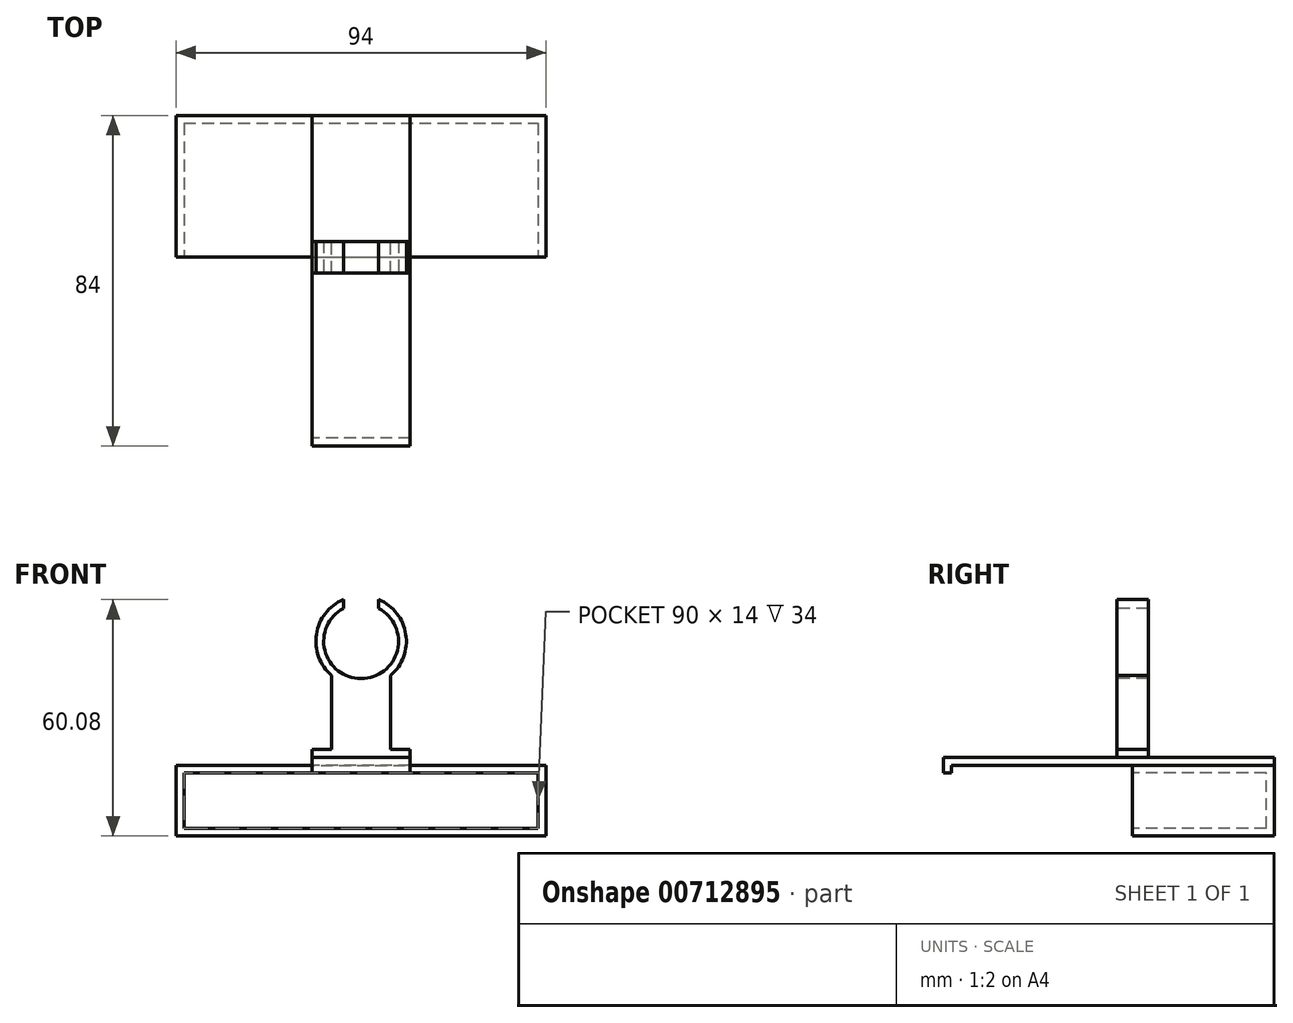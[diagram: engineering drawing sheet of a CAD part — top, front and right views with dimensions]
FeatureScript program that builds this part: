
annotation { "Feature Type Name" : "Feature", "Feature Type Description" : "" }
export const myFeature = defineFeature(function(context is Context, id is Id, definition is map)
    precondition{}
    {
        {
            var Q0;
            Q0=qCreatedBy(makeId("Front.planeOp"),FACE);
            var sketch = newSketch(context, id + "F0", { "sketchPlane" : qUnion([Q0])});
            skLineSegment(sketch, "E0.bottom", {"start": v(-47, 0) * mm, "end": v(47, 0) * mm});
            skLineSegment(sketch, "E0.top", {"start": v(-47, 18) * mm, "end": v(47, 18) * mm});
            skLineSegment(sketch, "E0.left", {"start": v(-47, 0) * mm, "end": v(-47, 18) * mm});
            skLineSegment(sketch, "E0.right", {"start": v(47, 0) * mm, "end": v(47, 18) * mm});
            skSolve(sketch);
        }
        {
            var Q0;
            Q0=makeQuery(id+"F0.imprint","IMPRINT",FACE,{"disambiguationData":[TD([[makeQuery(id+"F0.imprint","IMPRINT",EDGE,{"derivedFrom":sQuery(id+"F0.wireOp",EDGE,"E0.bottom")}),1.0]])]});
            extrude(context, id + "F1", {"entities" : qUnion([Q0]), "oppositeDirection" : true, "depth" : 36 * mm, "offsetDistance" : 25 * mm});
        }
        {
            var Q0;
            Q0=makeQuery(id+"F1.opExtrude","CAP_FACE",FACE,{"disambiguationData":[OSD([sQuery(id+"F0.wireOp",EDGE,"E0.bottom"),sQuery(id+"F0.wireOp",EDGE,"E0.top"),sQuery(id+"F0.wireOp",EDGE,"E0.left"),sQuery(id+"F0.wireOp",EDGE,"E0.right")])],"isStart":true});
            shell(context, id + "F2", {"entities" : qUnion([Q0]), "thickness" : 2 * mm});
        }
        {
            var Q0;
            Q0=qCreatedBy(makeId("Right.planeOp"),FACE);
            var sketch = newSketch(context, id + "F3", { "sketchPlane" : qUnion([Q0])});
            skLineSegment(sketch, "E1.0", {"start": v(36, 18) * mm, "end": v(0, 18) * mm});
            skLineSegment(sketch, "E2.0.1", {"start": v(0, 18) * mm, "end": v(36, 18) * mm});
            skLineSegment(sketch, "E3.bottom", {"start": v(36, 18) * mm, "end": v(-44.7, 18) * mm});
            skLineSegment(sketch, "E3.top", {"start": v(36, 20) * mm, "end": v(-48, 20) * mm});
            skLineSegment(sketch, "E3.left", {"start": v(36, 18) * mm, "end": v(36, 20) * mm});
            skLineSegment(sketch, "E3.right", {"start": v(-48, 18) * mm, "end": v(-48, 20) * mm});
            skLineSegment(sketch, "E4.top", {"start": v(-48, 16) * mm, "end": v(-46, 16) * mm});
            skLineSegment(sketch, "E4.left", {"start": v(-48, 18) * mm, "end": v(-48, 16) * mm});
            skLineSegment(sketch, "E4.right", {"start": v(-46, 18) * mm, "end": v(-46, 17) * mm});
            skLineSegment(sketch, "E5", {"start": v(-44.7, 18) * mm, "end": v(-46, 18) * mm});
            skLineSegment(sketch, "E6", {"start": v(-46, 17) * mm, "end": v(-46, 16) * mm});
            skSolve(sketch);
        }
        {
            var Q0;
            Q0 = qSketchRegion(id + "F3", true);
            extrude(context, id + "F4", {"entities" : qUnion([Q0]), "endBound" : BoundingType.SYMMETRIC, "depth" : 25 * mm, "offsetDistance" : 25 * mm});
        }
        {
            var Q0;
            Q0=qCreatedBy(makeId("Front.planeOp"),FACE);
            var sketch = newSketch(context, id + "F5", { "sketchPlane" : qUnion([Q0])});
            skLineSegment(sketch, "E7.0", {"start": v(12.5, 20) * mm, "end": v(-12.5, 20) * mm, "construction": true});
            skLineSegment(sketch, "E8.0", {"start": v(-12.5, 20) * mm, "end": v(-12.5, 16) * mm, "construction": true});
            skLineSegment(sketch, "E9.0", {"start": v(12.5, 20) * mm, "end": v(12.5, 16) * mm, "construction": true});
            skLineSegment(sketch, "E10.bottom", {"start": v(-12.5, 20) * mm, "end": v(12.5, 20) * mm});
            skLineSegment(sketch, "E10.top", {"start": v(-12.5, 22) * mm, "end": v(12.5, 22) * mm});
            skLineSegment(sketch, "E10.left", {"start": v(-12.5, 20) * mm, "end": v(-12.5, 22) * mm});
            skLineSegment(sketch, "E10.right", {"start": v(12.5, 20) * mm, "end": v(12.5, 22) * mm});
            skSolve(sketch);
        }
        {
            var Q0;
            Q0 = qSketchRegion(id + "F5", true);
            extrude(context, id + "F6", {"entities" : qUnion([Q0]), "endBound" : BoundingType.SYMMETRIC, "depth" : 8 * mm, "offsetDistance" : 25 * mm});
        }
        {
            var Q0;
            Q0=qCreatedBy(makeId("Front.planeOp"),FACE);
            var sketch = newSketch(context, id + "F7", { "sketchPlane" : qUnion([Q0])});
            skLineSegment(sketch, "E11.0", {"start": v(-12.5, 22) * mm, "end": v(0, 22) * mm, "construction": true});
            skLineSegment(sketch, "E12.0", {"start": v(0.2, 22) * mm, "end": v(12.5, 22) * mm, "construction": true});
            skArc(sketch, "E13.0", {"start": v(0.18, 27) * mm, "mid": v(0.1, 50) * mm, "end": v(0.03, 27) * mm, "construction": true});
            skLineSegment(sketch, "E14.0", {"start": v(-12.5, 20) * mm, "end": v(-12.5, 22) * mm, "construction": true});
            skLineSegment(sketch, "E15.0", {"start": v(12.5, 20) * mm, "end": v(12.5, 22) * mm, "construction": true});
            skLineSegment(sketch, "E16.bottom", {"start": v(-7.5, 47) * mm, "end": v(7.5, 47) * mm});
            skLineSegment(sketch, "E16.top", {"start": v(-7.5, 22) * mm, "end": v(7.5, 22) * mm});
            skLineSegment(sketch, "E16.left", {"start": v(-7.5, 47) * mm, "end": v(-7.5, 22) * mm});
            skLineSegment(sketch, "E16.right", {"start": v(7.5, 47) * mm, "end": v(7.5, 22) * mm});
            skSolve(sketch);
        }
        {
            var Q0;
            Q0 = qSketchRegion(id + "F7", true);
            extrude(context, id + "F8", {"entities" : qUnion([Q0]), "operationType" : NewBodyOperationType.ADD, "endBound" : BoundingType.SYMMETRIC, "depth" : 8 * mm, "offsetDistance" : 25 * mm});
        }
        {
            var Q0;
            Q0=qCreatedBy(makeId("Front.planeOp"),FACE);
            var sketch = newSketch(context, id + "F9", { "sketchPlane" : qUnion([Q0])});
            skLineSegment(sketch, "E17.0", {"start": v(-12.5, 22) * mm, "end": v(-7.5, 22) * mm, "construction": true});
            skLineSegment(sketch, "E18.0", {"start": v(-12.5, 20) * mm, "end": v(-12.5, 22) * mm, "construction": true});
            skLineSegment(sketch, "E19.0", {"start": v(12.5, 20) * mm, "end": v(12.5, 22) * mm, "construction": true});
            skCircle(sketch, "E20", {"center": v(0, 49.5) * mm, "radius": 11.5 * mm});
            skPoint(sketch, "E20.first.point", {"position": v(0, 38) * mm});
            skPoint(sketch, "E20.second.point", {"position": v(-10, 43.82) * mm});
            skPoint(sketch, "E20.second.point.positionSnap0", {"position": v(-10, 22) * mm});
            skPoint(sketch, "E20.third.point", {"position": v(-10.78, 53.5) * mm});
            skLineSegment(sketch, "E21.0.0", {"start": v(-7.5, 22) * mm, "end": v(-12.5, 22) * mm, "construction": true});
            skLineSegment(sketch, "E21.0.1", {"start": v(-12.5, 22) * mm, "end": v(-12.5, 20) * mm, "construction": true});
            skLineSegment(sketch, "E21.0.2", {"start": v(-12.5, 20) * mm, "end": v(12.5, 20) * mm, "construction": true});
            skLineSegment(sketch, "E22.0", {"start": v(-47, 18) * mm, "end": v(47, 18) * mm, "construction": true});
            skSolve(sketch);
        }
        {
            var Q0;
            Q0 = qSketchRegion(id + "F9", true);
            extrude(context, id + "F10", {"entities" : qUnion([Q0]), "operationType" : NewBodyOperationType.ADD, "endBound" : BoundingType.SYMMETRIC, "depth" : 8 * mm, "offsetDistance" : 25 * mm});
        }
        {
            var Q0;
            Q0=qCreatedBy(makeId("Front.planeOp"),FACE);
            var sketch = newSketch(context, id + "F11", { "sketchPlane" : qUnion([Q0])});
            skCircle(sketch, "E23", {"center": v(0, 49.5) * mm, "radius": 9.5 * mm});
            skCircle(sketch, "E24.0", {"center": v(0, 49.5) * mm, "radius": 11.5 * mm, "construction": true});
            skSolve(sketch);
        }
        {
            var Q0;
            Q0 = qSketchRegion(id + "F11", true);
            extrude(context, id + "F12", {"entities" : qUnion([Q0]), "operationType" : NewBodyOperationType.REMOVE, "endBound" : BoundingType.SYMMETRIC, "oppositeDirection" : true, "depth" : 35.4 * mm, "offsetDistance" : 25 * mm});
        }
        {
            var Q0;
            Q0=qCreatedBy(makeId("Front.planeOp"),FACE);
            var sketch = newSketch(context, id + "F13", { "sketchPlane" : qUnion([Q0])});
            skLineSegment(sketch, "E25.0", {"start": v(-7.5, 22) * mm, "end": v(-7.5, 22) * mm});
            skLineSegment(sketch, "E26.bottom", {"start": v(-4.5, 72) * mm, "end": v(4.5, 72) * mm});
            skLineSegment(sketch, "E26.top", {"start": v(-4.5, 47) * mm, "end": v(4.5, 47) * mm});
            skLineSegment(sketch, "E26.left", {"start": v(-4.5, 72) * mm, "end": v(-4.5, 47) * mm});
            skLineSegment(sketch, "E26.right", {"start": v(4.5, 72) * mm, "end": v(4.5, 47) * mm});
            skSolve(sketch);
        }
        {
            var Q0;
            Q0 = qSketchRegion(id + "F13", true);
            extrude(context, id + "F14", {"entities" : qUnion([Q0]), "operationType" : NewBodyOperationType.REMOVE, "endBound" : BoundingType.SYMMETRIC, "oppositeDirection" : true, "depth" : 25 * mm, "offsetDistance" : 25 * mm});
        }
    });
